# Revit family: DATABAR Double Outlet Tap Off Unit
name_source: partatom
category: Electrical Equipment
revit_build: Autodesk Revit 2018 (Build: 20190510_1515(x64)
units: mm (PartAtom-declared; Revit-internal decimal feet)

## family parameters
Cut with Voids When Loaded = No
Host = Face
OmniClass Number = 23.80.30.11.17
OmniClass Title = Distribution Boards and Control Panels
Panel Configuration = Two Columns, Circuits Across
Part Type = Panelboard
Room Calculation Point = No
Round Connector Dimension = Use Diameter
Shared = No

## types (12) — shared parameters
AMG_Tap_Off_Width = 165 mm
Handle 1 Visible = Yes
Manufacturer = Anord Mardix
URL = https://anordmardix.com
Version = A
zero-valued in all types: Default Elevation

## per-type parameters (varying)
| type | AMG_Socket1 Dist | AMG_Socket2 Dist | AMG_Tap_Off_Height | AMG_Tap_Off_Length | AMG_Tap_Off_Socket_Height | Description | Handle 2 Visible | Handle 3 Visible |
| Double Outlet 16A - SP | 50 mm  [stored 0.164042 ft] | 100 mm  [stored 0.328084 ft] | 98 mm  [stored 0.321522 ft] | 290 mm  [stored 0.951444 ft] | 55 mm  [stored 0.180446 ft] | Tap Off Unit, Double Outlet, 16A, SP | Yes | No |
| Double Outlet 32A - SP | 50 mm  [stored 0.164042 ft] | 100 mm  [stored 0.328084 ft] | 98 mm  [stored 0.321522 ft] | 290 mm  [stored 0.951444 ft] | 64 mm  [stored 0.209974 ft] | Tap Off Unit, Double Outlet, 32A, SP | Yes | No |
| Double Outlet 63A - SP | 50 mm  [stored 0.164042 ft] | 100 mm  [stored 0.328084 ft] | 98 mm  [stored 0.321522 ft] | 290 mm  [stored 0.951444 ft] | 80 mm  [stored 0.262467 ft] | Tap Off Unit, Double Outlet, 63A, SP | Yes | No |
| Double Outlet 16A - TP | 80 mm  [stored 0.262467 ft] | 130 mm  [stored 0.426509 ft] | 98 mm  [stored 0.321522 ft] | 370 mm  [stored 1.21391 ft] | 55 mm  [stored 0.180446 ft] | Tap Off Unit, Double Outlet, 16A, TP | No | Yes |
| Double Outlet 32A - TP | 80 mm  [stored 0.262467 ft] | 130 mm  [stored 0.426509 ft] | 98 mm  [stored 0.321522 ft] | 370 mm  [stored 1.21391 ft] | 64 mm  [stored 0.209974 ft] | Tap Off Unit, Double Outlet, 32A, TP | No | Yes |
| Double Outlet 63A - TP | 80 mm  [stored 0.262467 ft] | 130 mm  [stored 0.426509 ft] | 98 mm  [stored 0.321522 ft] | 370 mm  [stored 1.21391 ft] | 80 mm  [stored 0.262467 ft] | Tap Off Unit, Double Outlet, 63A, TP | No | Yes |
| Double Outlet 16A - SP&Meter | 80 mm  [stored 0.262467 ft] | 130 mm  [stored 0.426509 ft] | 98 mm  [stored 0.321522 ft] | 370 mm  [stored 1.21391 ft] | 55 mm  [stored 0.180446 ft] | Tap Off Unit, Double Outlet, 16A, SP&Meter | No | Yes |
| Double Outlet 32A - SP&Meter | 80 mm  [stored 0.262467 ft] | 130 mm  [stored 0.426509 ft] | 98 mm  [stored 0.321522 ft] | 370 mm  [stored 1.21391 ft] | 64 mm  [stored 0.209974 ft] | Tap Off Unit, Double Outlet, 32A, SP&Meter | No | Yes |
| Double Outlet 63A - SP&Meter | 80 mm  [stored 0.262467 ft] | 130 mm  [stored 0.426509 ft] | 98 mm  [stored 0.321522 ft] | 370 mm  [stored 1.21391 ft] | 80 mm  [stored 0.262467 ft] | Tap Off Unit, Double Outlet, 63A, SP&Meter | No | Yes |
| Double Outlet 16A - TP&Meter | 80 mm  [stored 0.262467 ft] | 130 mm  [stored 0.426509 ft] | 182 mm  [stored 0.597113 ft] | 370 mm  [stored 1.21391 ft] | 55 mm  [stored 0.180446 ft] | Tap Off Unit, Double Outlet, 16A, TP&Meter | No | Yes |
| Double Outlet 32A - TP&Meter | 80 mm  [stored 0.262467 ft] | 130 mm  [stored 0.426509 ft] | 182 mm  [stored 0.597113 ft] | 370 mm  [stored 1.21391 ft] | 64 mm  [stored 0.209974 ft] | Tap Off Unit, Double Outlet, 32A, TP&Meter | No | Yes |
| Double Outlet 63A - TP&Meter | 80 mm  [stored 0.262467 ft] | 130 mm  [stored 0.426509 ft] | 182 mm  [stored 0.597113 ft] | 370 mm  [stored 1.21391 ft] | 80 mm  [stored 0.262467 ft] | Tap Off Unit, Double Outlet, 32A, TP&Meter | No | Yes |

note: [stored X ft] marks values corroborated as IEEE doubles in the binary element streams (Revit-internal decimal feet)

## geometry (parser evidence)
native form markers: Sweep x11
no freeform markers — native parametric forms only
